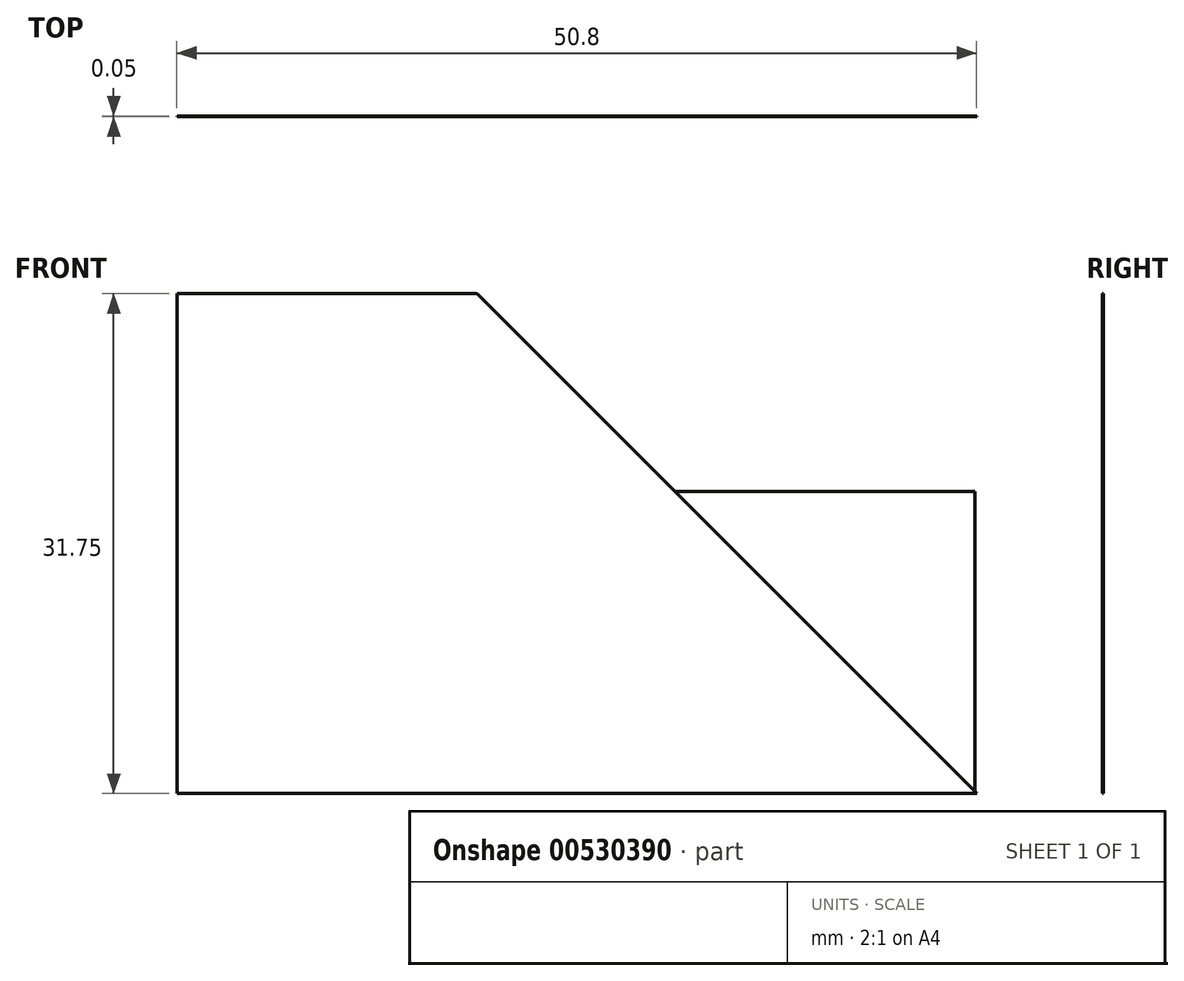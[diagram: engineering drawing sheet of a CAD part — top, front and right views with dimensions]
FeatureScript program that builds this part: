
annotation { "Feature Type Name" : "Feature", "Feature Type Description" : "" }
export const myFeature = defineFeature(function(context is Context, id is Id, definition is map)
    precondition{}
    {
        {
            var Q0;
            Q0=qCreatedBy(makeId("Front.planeOp"),FACE);
            var sketch = newSketch(context, id + "F0", { "sketchPlane" : qUnion([Q0])});
            skLineSegment(sketch, "E0", {"start": v(-35.03, 34.04) * mm, "end": v(-35.03, 2.29) * mm});
            skLineSegment(sketch, "E1", {"start": v(-35.03, 2.29) * mm, "end": v(15.77, 2.29) * mm});
            skLineSegment(sketch, "E2", {"start": v(15.77, 2.29) * mm, "end": v(-15.98, 34.04) * mm});
            skLineSegment(sketch, "E3", {"start": v(-15.98, 34.04) * mm, "end": v(-35.03, 34.04) * mm});
            skSolve(sketch);
        }
        {
            var Q0;
            Q0=makeQuery(id+"F0.imprint","IMPRINT",FACE,{"disambiguationData":[TD([[makeQuery(id+"F0.imprint","IMPRINT",EDGE,{"derivedFrom":sQuery(id+"F0.wireOp",EDGE,"E0")}),1.0]])]});
            extrude(context, id + "F1", {"entities" : qUnion([Q0]), "depth" : 5 / 101.6 * mm, "offsetDistance" : 25.4 * mm});
        }
        {
            var Q0;
            Q0=qCreatedBy(makeId("Front.planeOp"),FACE);
            var sketch = newSketch(context, id + "F2", { "sketchPlane" : qUnion([Q0])});
            skLineSegment(sketch, "E4", {"start": v(15.66, 2.44) * mm, "end": v(-3.4, 2.44) * mm});
            skLineSegment(sketch, "E5", {"start": v(-3.4, 2.44) * mm, "end": v(-3.4, 21.49) * mm});
            skLineSegment(sketch, "E6", {"start": v(-3.4, 21.49) * mm, "end": v(15.66, 2.44) * mm});
            skLineSegment(sketch, "E7", {"start": v(15.66, 2.44) * mm, "end": v(15.66, 21.49) * mm});
            skLineSegment(sketch, "E8", {"start": v(15.66, 21.49) * mm, "end": v(-3.4, 21.49) * mm});
            skSolve(sketch);
        }
        {
            var Q0;
            Q0=makeQuery(id+"F2.imprint","IMPRINT",FACE,{"disambiguationData":[TD([[makeQuery(id+"F2.imprint","IMPRINT",EDGE,{"derivedFrom":sQuery(id+"F2.wireOp",EDGE,"E6")}),1.0]])]});
            extrude(context, id + "F3", {"entities" : qUnion([Q0]), "operationType" : NewBodyOperationType.ADD, "depth" : 3 / 101.6 * mm, "offsetDistance" : 25.4 * mm});
        }
    });
